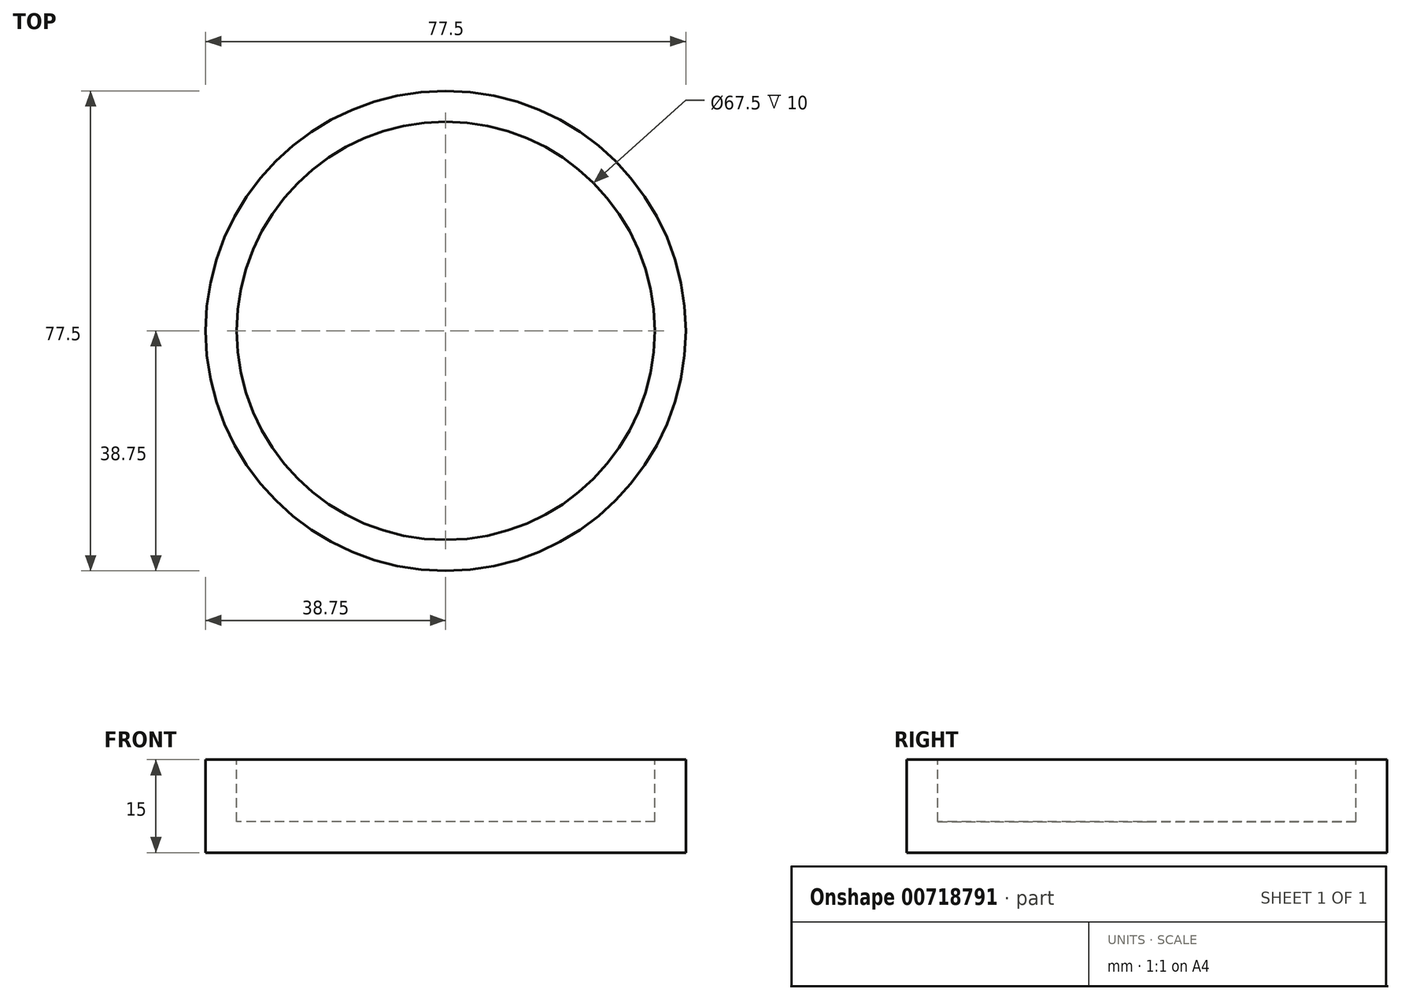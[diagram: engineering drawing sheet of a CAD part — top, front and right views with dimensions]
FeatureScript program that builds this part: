
annotation { "Feature Type Name" : "Feature", "Feature Type Description" : "" }
export const myFeature = defineFeature(function(context is Context, id is Id, definition is map)
    precondition{}
    {
        {
            var Q0;
            Q0=qCreatedBy(makeId("Top.planeOp"),FACE);
            var sketch = newSketch(context, id + "F0", { "sketchPlane" : qUnion([Q0])});
            skCircle(sketch, "E0", {"center": v(0, 0) * mm, "radius": 33.75 * mm, "construction": true});
            skCircle(sketch, "E1", {"center": v(0, 0) * mm, "radius": 38.75 * mm});
            skSolve(sketch);
        }
        {
            var Q0;
            Q0 = qSketchRegion(id + "F0", true);
            extrude(context, id + "F1", {"entities" : qUnion([Q0]), "depth" : 15 * mm, "offsetDistance" : 25 * mm});
        }
        {
            var Q0;
            Q0=makeQuery(id+"F1.opExtrude","CAP_FACE",FACE,{"disambiguationData":[OSD([sQuery(id+"F0.wireOp",EDGE,"E1")])],"isStart":false});
            var sketch = newSketch(context, id + "F2", { "sketchPlane" : qUnion([Q0])});
            skCircle(sketch, "E2", {"center": v(0, 0) * mm, "radius": 33.75 * mm});
            skSolve(sketch);
        }
        {
            var Q0;
            Q0 = qSketchRegion(id + "F2", true);
            extrude(context, id + "F3", {"entities" : qUnion([Q0]), "operationType" : NewBodyOperationType.REMOVE, "oppositeDirection" : true, "depth" : 10 * mm, "offsetDistance" : 25 * mm});
        }
    });
